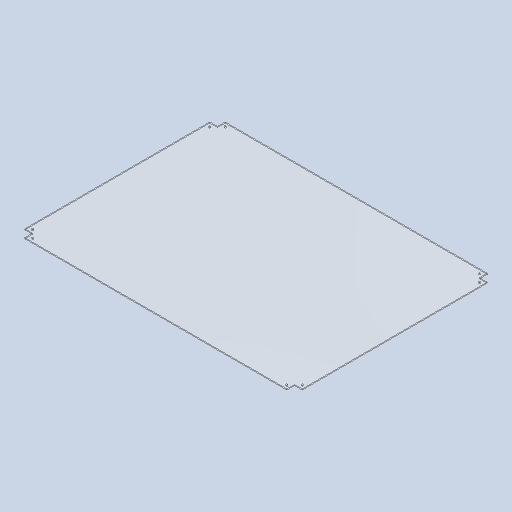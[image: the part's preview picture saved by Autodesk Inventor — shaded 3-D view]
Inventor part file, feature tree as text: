
AUTODESK INVENTOR PART (.ipt)
format: ipt  version: 2023 (Build 270158000, 158)  size: 253,952 bytes
history: native  units: in
note: dims shown in document units (in); Inventor stores cm internally (conversion verified against a paired STEP export)
features: extrude x1, sketch x1
ambient origin geometry x8: Origin, YZ Plane, XZ Plane, XY Plane, X Axis, Y Axis, Z Axis, Center Point
bodies: Solid1 (feature_tree)
feature tree (2):
  extrude  "Extrusion1"  Depth=26.0in
  sketch  "Sketch1"  dims[d0=36.0in d1=26.0in d2=1.0in d3=1.0in d4=1.0in d5=1.0in d6=1.0in d7=1.0in d8=1.0in d9=1.0in d10=0.1969in d11=0.5in d12=0.5in d13=0.1969in d14=0.5in d15=0.5in d16=0.1969in d17=0.1969in d18=0.5in d19=0.5in d20=0.5in d21=0.5in d22=0.125in d23=0.0in]
